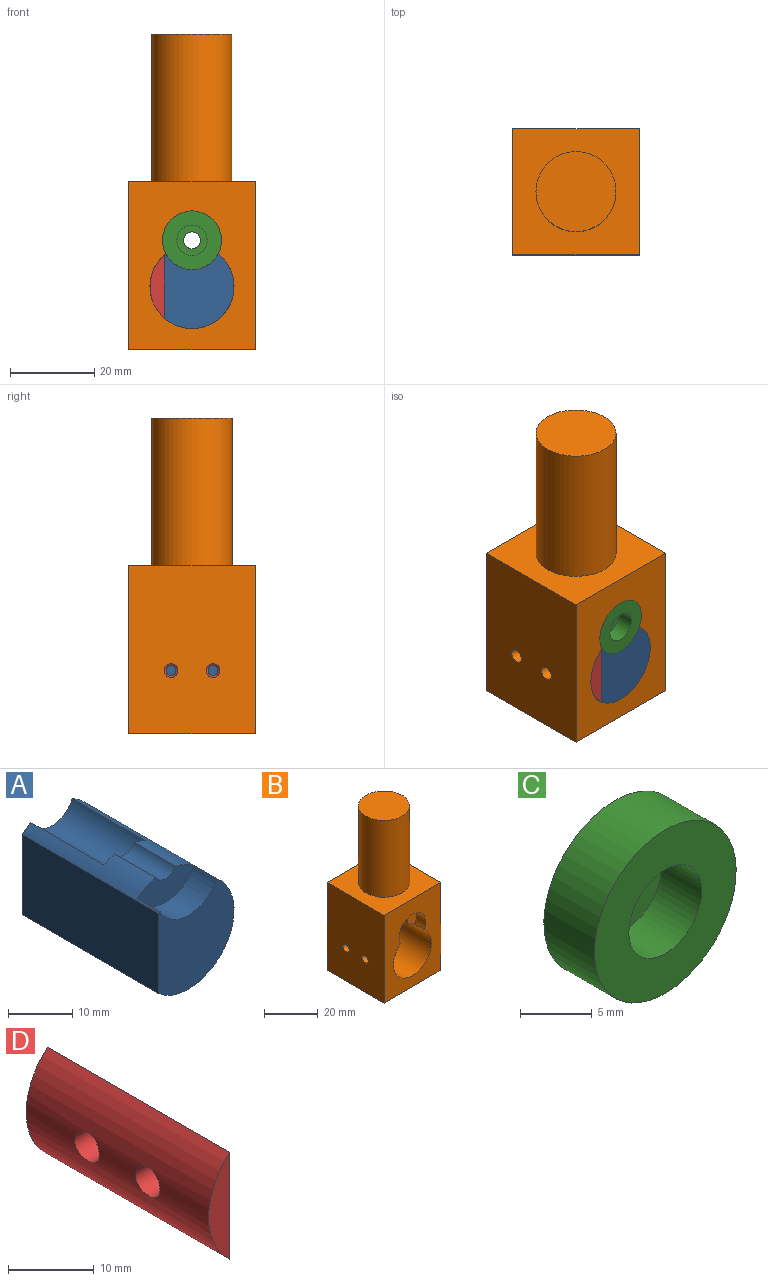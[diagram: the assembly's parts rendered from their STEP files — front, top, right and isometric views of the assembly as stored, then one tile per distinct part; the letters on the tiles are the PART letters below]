
ASSEMBLY  parts=4 mates=5
PART A: 16 faces, bbox 16.5x30x19.8 mm
  f0: cylinder r=10mm len=30mm, axis (0,1,0), area 940.3mm2, adj f1,f2,f3,f5,f6,f7,f8,f9
  f1: plane 17.82x16.5mm, normal (0,-1,0), area 224.6mm2, adj f0,f4,f5,f9
  f2: cylinder r=2.5mm len=9mm, axis (0,-1,0), area 47.4mm2, adj f0,f4,f6,f7
  f3: plane 18.91x16.5mm, normal (0,1,0), area 251.6mm2, adj f0,f4,f8,f9
  f4: cylinder r=10mm len=30mm, axis (0,1,0), area 83.5mm2, adj f1,f2,f3,f5,f6,f7,f8,f9
  f5: cylinder r=7mm len=12.47mm, axis (0,-1,0), area 76.9mm2, adj f0,f1,f4,f6
  f6: plane 12.47x5.76mm, normal (0,-1,0), area 48mm2, adj f0,f2,f4,f5
  f7: plane 9.08x3.76mm, normal (0,1,0), area 21.1mm2, adj f0,f2,f4,f8
  f8: cylinder r=5mm len=16mm, axis (0,1,0), area 182.3mm2, adj f0,f3,f4,f7
  f9: plane 30x15.2mm, normal (-1,0,0), area 456mm2, adj f0,f1,f3,f4
  f10: cylinder r=3mm len=13mm, axis (0,0,-1), area 240.7mm2, adj f0,f11
  f11: cone r=0mm half-angle=59deg, axis (0,0,-1), area 33mm2, adj f10
  f12: cylinder r=3mm len=13mm, axis (0,0,-1), area 240.7mm2, adj f0,f13
  f13: cone r=0mm half-angle=59deg, axis (0,0,-1), area 33mm2, adj f12
  f14: cylinder r=3mm len=13mm, axis (0,0,-1), area 240.7mm2, adj f0,f15
  f15: cone r=0mm half-angle=59deg, axis (0,0,-1), area 33mm2, adj f14
PART B: 16 faces, bbox 30x30x75 mm
  f0: cylinder r=10mm len=30mm, axis (0,-1,0), area 1665.7mm2, adj f1,f2,f5,f7,f8,f12,f13,f14
  f1: plane 14x10.18mm, normal (0,-1,0), area 86.3mm2, adj f0,f12,f15
  f2: plane 40x30mm, normal (0,1,0), area 833mm2, adj f0,f3,f4,f6,f9,f13
  f3: plane 40x30mm, normal (1,0,0), area 1200mm2, adj f2,f5,f6,f9
  f4: plane 40x30mm, normal (-1,0,0), area 1182.9mm2, adj f2,f5,f6,f7,f8,f9
  f5: plane 40x30mm, normal (0,-1,0), area 784.5mm2, adj f0,f3,f4,f6,f9,f12
  f6: plane 30x30mm, normal (0,0,-1), area 900mm2, adj f2,f3,f4,f5
  f7: cylinder r=1.65mm len=5.14mm, axis (-1,0,0), area 52.5mm2, adj f0,f4
  f8: cylinder r=1.65mm len=5.14mm, axis (-1,0,0), area 52.5mm2, adj f0,f4
  f9: plane 30x30mm, normal (0,0,1), area 615mm2, adj f2,f3,f4,f5,f10
  f10: cylinder r=9.53mm len=35mm, axis (0,0,-1), area 2094.7mm2, adj f9,f11
  f11: plane 19.05x19.05mm, normal (0,0,1), area 285mm2, adj f10
  f12: cylinder r=7mm len=14mm, axis (0,-1,0), area 143mm2, adj f0,f1,f5
  f13: cylinder r=5mm len=10mm, axis (0,1,0), area 100.1mm2, adj f0,f2,f14
  f14: plane 10x7.09mm, normal (0,1,0), area 37.8mm2, adj f0,f13,f15
  f15: cylinder r=2.5mm len=20mm, axis (0,-1,0), area 208.9mm2, adj f0,f1,f14
PART C: 6 faces, bbox 14x5x14 mm
  f0: cylinder r=2mm len=4mm, axis (0,-1,0), area 12.6mm2, adj f3,f5
  f1: cylinder r=7mm len=14mm, axis (0,1,0), area 219.9mm2, adj f2,f3
  f2: plane 14x14mm, normal (0,-1,0), area 113.2mm2, adj f1,f4
  f3: plane 14x14mm, normal (0,1,0), area 141.4mm2, adj f0,f1
  f4: cylinder r=3.6mm len=7.2mm, axis (0,-1,0), area 90.5mm2, adj f2,f5
  f5: plane 7.2x7.2mm, normal (0,-1,0), area 28.1mm2, adj f0,f4
PART D: 8 faces, bbox 3.5x30x15.2 mm
  f0: cylinder r=10mm len=30mm, axis (0,1,0), area 492.7mm2, adj f1,f2,f3,f4,f6
  f1: plane 30x15.2mm, normal (1,0,0), area 447.4mm2, adj f0,f2,f3,f5,f7
  f2: plane 15.2x3.5mm, normal (0,-1,0), area 36.9mm2, adj f0,f1
  f3: plane 15.2x3.5mm, normal (0,1,0), area 36.9mm2, adj f0,f1
  f4: cylinder r=2mm len=4mm, axis (-1,0,0), area 36.4mm2, adj f0,f5
  f5: cone r=0mm half-angle=59deg, axis (-1,0,0), area 9.7mm2, adj f1,f4
  f6: cylinder r=2mm len=4mm, axis (-1,0,0), area 36.4mm2, adj f0,f7
  f7: cone r=0mm half-angle=59deg, axis (-1,0,0), area 9.7mm2, adj f1,f6
PLACE A rot(axis=(-0.2,0.01,0.98),0deg) t=(-57.86,2.54,19.67)mm
PLACE B rot(axis=(-0.2,0.01,0.98),0deg) t=(-57.86,2.54,44.67)mm
PLACE C rot(axis=(-0.2,0,0.98),0deg) t=(-57.86,-7.46,30.67)mm
PLACE D rot(axis=(-0.2,0.01,0.98),0deg) t=(-57.86,2.54,19.67)mm
MATE planar B.f1 <-> C.f0  axis (0,-1,0) through (-60.03,-7.46,29.43)mm
MATE revolute A.f0 <-> B.f0  axis (0,1,0) through (-57.86,2.54,19.67)mm
MATE cylindrical B.f12 <-> C.f4  axis (0,-1,0) through (-57.86,-12.46,30.67)mm
MATE cylindrical B.f8 <-> D.f6  axis (-1,0,0) through (-72.86,7.54,19.67)mm
MATE cylindrical D.f0 <-> B.f0  axis (0,-1,0) through (-57.86,-12.46,19.67)mm
